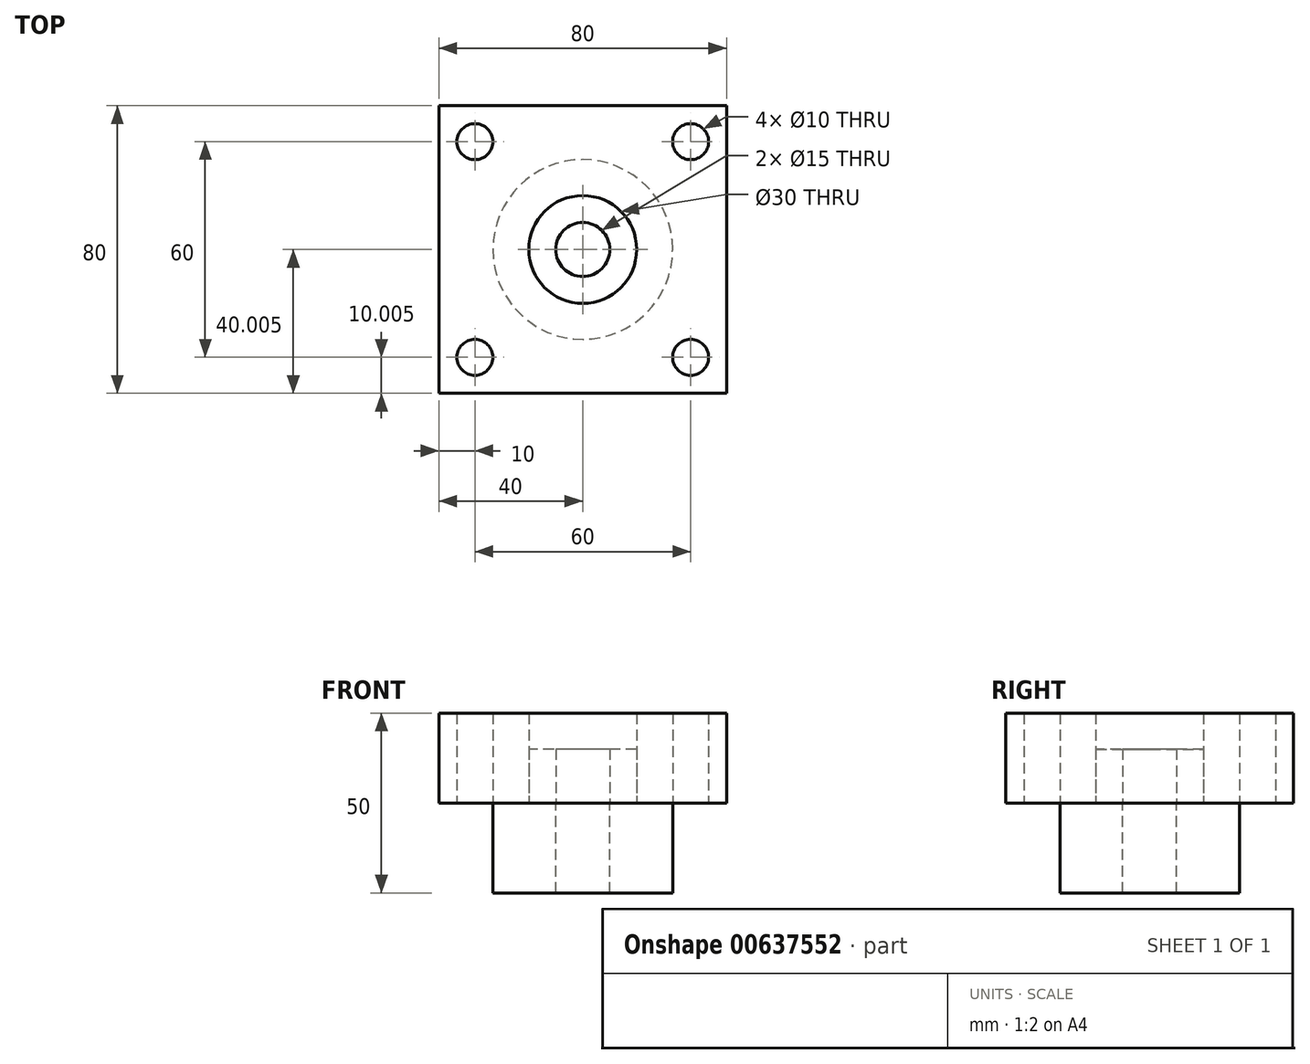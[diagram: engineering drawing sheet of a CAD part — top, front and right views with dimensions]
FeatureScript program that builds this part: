
annotation { "Feature Type Name" : "Feature", "Feature Type Description" : "" }
export const myFeature = defineFeature(function(context is Context, id is Id, definition is map)
    precondition{}
    {
        {
            var Q0;
            Q0=qCreatedBy(makeId("Top.planeOp"),FACE);
            var sketch = newSketch(context, id + "F0", { "sketchPlane" : qUnion([Q0])});
            skCircle(sketch, "E0", {"center": v(-5.57, -1.96) * mm, "radius": 15 * mm});
            skCircle(sketch, "E1", {"center": v(-5.57, -1.96) * mm, "radius": 7.5 * mm});
            skPoint(sketch, "E2.end.orphan", {"position": v(34.43, -1.96) * mm});
            skPoint(sketch, "E3.orphan", {"position": v(34.43, -41.96) * mm});
            skPoint(sketch, "E4.start.orphan", {"position": v(-45.57, -1.96) * mm});
            skPoint(sketch, "E5.end.orphan", {"position": v(-45.57, -41.96) * mm});
            skPoint(sketch, "E5.start.orphan", {"position": v(-5.57, -41.96) * mm});
            skPoint(sketch, "E6.start.orphan", {"position": v(-5.57, 38.04) * mm});
            skPoint(sketch, "E7.orphan", {"position": v(-45.57, 38.04) * mm});
            skPoint(sketch, "E8.end.orphan", {"position": v(34.43, 38.04) * mm});
            skSolve(sketch);
        }
        {
            var Q0;
            {var subQ0=sQuery(id+"F0.wireOp",EDGE,"E0");var subQ1=sQuery(id+"F0.wireOp",EDGE,"E6");var subQ2=makeQuery(id+"F0.imprint","INTERSECT",VERTEX,{"disambiguationData":[OD(0.0)],"derivedFrom":[subQ1,subQ0]});Q0=makeQuery(id+"F0.imprint","IMPRINT",FACE,{"disambiguationData":[TD([[makeQuery(id+"F0.imprint","IMPRINT",EDGE,{"disambiguationData":[TD([[subQ2,-1.0]])],"derivedFrom":subQ1}),1.0]])]});}
            var Q1;
            {var subQ0=sQuery(id+"F0.wireOp",EDGE,"E0");var subQ1=sQuery(id+"F0.wireOp",EDGE,"E6");var subQ2=makeQuery(id+"F0.imprint","INTERSECT",VERTEX,{"disambiguationData":[OD(0.0)],"derivedFrom":[subQ1,subQ0]});Q1=makeQuery(id+"F0.imprint","IMPRINT",FACE,{"disambiguationData":[TD([[makeQuery(id+"F0.imprint","IMPRINT",EDGE,{"disambiguationData":[TD([[subQ2,-1.0]])],"derivedFrom":subQ1}),-1.0]])]});}
            var Q2;
            {var subQ0=sQuery(id+"F0.wireOp",EDGE,"E1");var subQ1=sQuery(id+"F0.wireOp",EDGE,"E6");var subQ2=makeQuery(id+"F0.imprint","INTERSECT",VERTEX,{"disambiguationData":[OD(1.0)],"derivedFrom":[subQ1,subQ0]});Q2=makeQuery(id+"F0.imprint","IMPRINT",FACE,{"disambiguationData":[TD([[makeQuery(id+"F0.imprint","IMPRINT",EDGE,{"disambiguationData":[TD([[subQ2,-1.0]])],"derivedFrom":subQ1}),-1.0]])]});}
            var Q3;
            {var subQ0=sQuery(id+"F0.wireOp",EDGE,"E1");var subQ1=sQuery(id+"F0.wireOp",EDGE,"E6");var subQ2=makeQuery(id+"F0.imprint","INTERSECT",VERTEX,{"disambiguationData":[OD(1.0)],"derivedFrom":[subQ1,subQ0]});Q3=makeQuery(id+"F0.imprint","IMPRINT",FACE,{"disambiguationData":[TD([[makeQuery(id+"F0.imprint","IMPRINT",EDGE,{"disambiguationData":[TD([[subQ2,-1.0]])],"derivedFrom":subQ1}),1.0]])]});}
            var Q4;
            Q4=makeQuery(id+"F0.imprint","IMPRINT",FACE,{"disambiguationData":[TD([[makeQuery(id+"F0.imprint","IMPRINT",EDGE,{"derivedFrom":sQuery(id+"F0.wireOp",EDGE,"E0")}),1.0]])]});
            extrude(context, id + "F1", {"entities" : qUnion([Q0, Q1, Q2, Q3, Q4]), "depth" : 15 * mm, "offsetDistance" : 25 * mm});
        }
        {
            var Q0;
            Q0=makeQuery(id+"F1.opExtrude","CAP_FACE",FACE,{"disambiguationData":[OSD([sQuery(id+"F0.wireOp",EDGE,"E0"),sQuery(id+"F0.wireOp",EDGE,"E1")])],"isStart":true});
            var sketch = newSketch(context, id + "F2", { "sketchPlane" : qUnion([Q0])});
            skLineSegment(sketch, "E9", {"start": v(-45.57, 41.96) * mm, "end": v(-45.57, -38.04) * mm});
            skLineSegment(sketch, "E10", {"start": v(-45.57, -38.04) * mm, "end": v(34.43, -38.04) * mm});
            skLineSegment(sketch, "E11", {"start": v(34.43, -38.04) * mm, "end": v(34.43, 41.96) * mm});
            skLineSegment(sketch, "E12", {"start": v(34.43, 41.96) * mm, "end": v(-45.57, 41.96) * mm});
            skCircle(sketch, "E13", {"center": v(-35.57, 31.96) * mm, "radius": 5 * mm});
            skCircle(sketch, "E14", {"center": v(24.43, 31.96) * mm, "radius": 5 * mm});
            skCircle(sketch, "E15", {"center": v(-35.57, -28.04) * mm, "radius": 5 * mm});
            skCircle(sketch, "E16", {"center": v(24.43, -28.04) * mm, "radius": 5 * mm});
            skCircle(sketch, "E17", {"center": v(-5.57, 1.96) * mm, "radius": 15 * mm});
            skSolve(sketch);
        }
        {
            var Q0;
            Q0=makeQuery(id+"F2.imprint","IMPRINT",FACE,{"disambiguationData":[TD([[makeQuery(id+"F2.imprint","IMPRINT",EDGE,{"derivedFrom":sQuery(id+"F2.wireOp",EDGE,"E9")}),1.0]])]});
            extrude(context, id + "F3", {"entities" : qUnion([Q0]), "oppositeDirection" : true, "depth" : 25 * mm, "offsetDistance" : 25 * mm});
        }
        {
            var Q0;
            Q0=makeQuery(id+"F3.opExtrude","CAP_FACE",FACE,{"disambiguationData":[OSD([sQuery(id+"F2.wireOp",EDGE,"E9"),sQuery(id+"F2.wireOp",EDGE,"E10"),sQuery(id+"F2.wireOp",EDGE,"E11"),sQuery(id+"F2.wireOp",EDGE,"E12"),sQuery(id+"F2.wireOp",EDGE,"E13"),sQuery(id+"F2.wireOp",EDGE,"E14"),sQuery(id+"F2.wireOp",EDGE,"E15"),sQuery(id+"F2.wireOp",EDGE,"E16"),sQuery(id+"F2.wireOp",EDGE,"E17")])],"isStart":true});
            var sketch = newSketch(context, id + "F4", { "sketchPlane" : qUnion([Q0])});
            skCircle(sketch, "E18", {"center": v(-5.57, 1.96) * mm, "radius": 25 * mm});
            skCircle(sketch, "E19", {"center": v(-5.57, 1.96) * mm, "radius": 7.5 * mm});
            skSolve(sketch);
        }
        {
            var Q0;
            Q0 = qSketchRegion(id + "F4", true);
            extrude(context, id + "F5", {"entities" : qUnion([Q0]), "depth" : 25 * mm, "offsetDistance" : 25 * mm});
        }
    });
